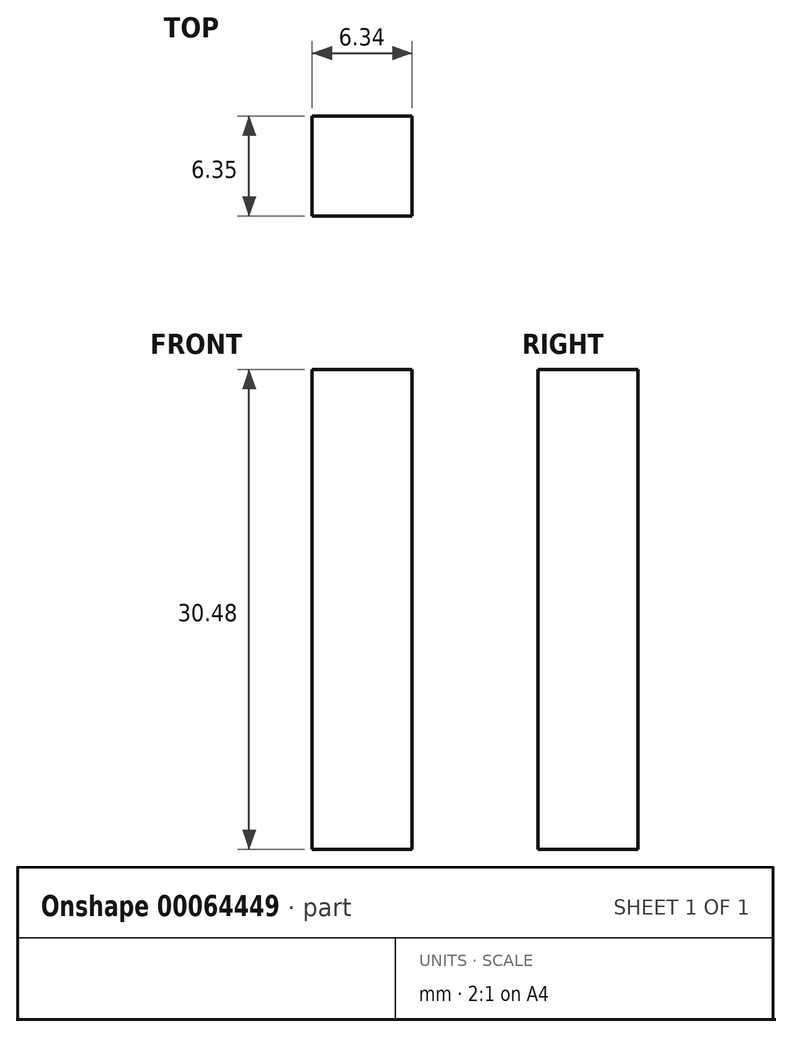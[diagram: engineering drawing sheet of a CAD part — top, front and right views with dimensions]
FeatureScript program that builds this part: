
annotation { "Feature Type Name" : "Feature", "Feature Type Description" : "" }
export const myFeature = defineFeature(function(context is Context, id is Id, definition is map)
    precondition{}
    {
        {
            var Q0;
            Q0=qCreatedBy(makeId("Front.planeOp"),FACE);
            var sketch = newSketch(context, id + "F0", { "sketchPlane" : qUnion([Q0])});
            skLineSegment(sketch, "E0.rect.bottom", {"start": v(3.18, 15.24) * mm, "end": v(-3.17, 15.24) * mm});
            skLineSegment(sketch, "E0.rect.top", {"start": v(3.18, -15.24) * mm, "end": v(-3.18, -15.24) * mm});
            skLineSegment(sketch, "E0.rect.left", {"start": v(3.18, 15.24) * mm, "end": v(3.18, -15.24) * mm});
            skLineSegment(sketch, "E0.rect.right", {"start": v(-3.17, 15.24) * mm, "end": v(-3.18, -15.24) * mm});
            skPoint(sketch, "E0.rect.middle", {"position": v(0, 0) * mm});
            skSolve(sketch);
        }
        {
            var Q0;
            Q0 = qSketchRegion(id + "F0", true);
            extrude(context, id + "F1", {"entities" : qUnion([Q0]), "depth" : 6.35 * mm});
        }
    });
